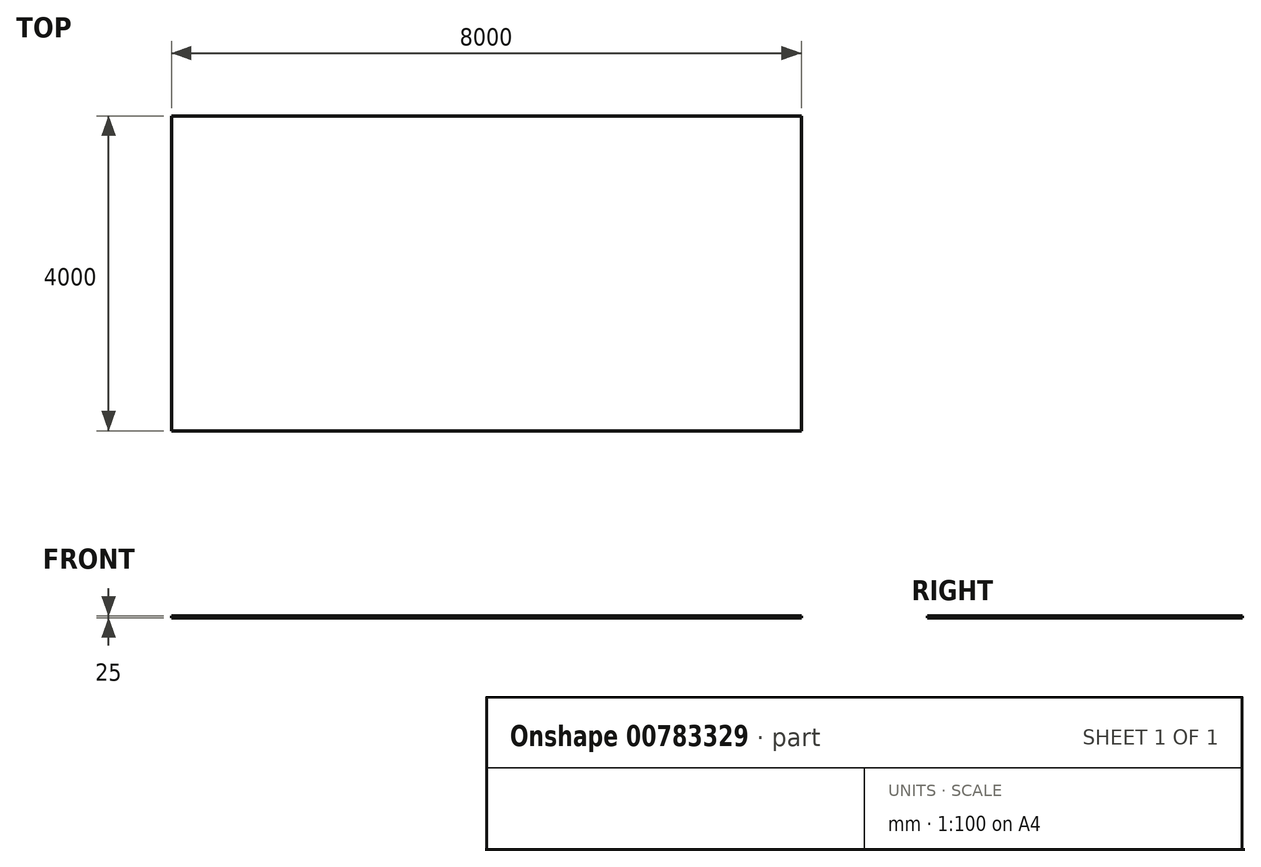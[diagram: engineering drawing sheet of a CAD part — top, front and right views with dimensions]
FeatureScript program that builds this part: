
annotation { "Feature Type Name" : "Feature", "Feature Type Description" : "" }
export const myFeature = defineFeature(function(context is Context, id is Id, definition is map)
    precondition{}
    {
        {
            var Q0;
            Q0=qCreatedBy(makeId("Top.planeOp"),FACE);
            var sketch = newSketch(context, id + "F0", { "sketchPlane" : qUnion([Q0])});
            skLineSegment(sketch, "E0.bottom", {"start": v(0, 0) * mm, "end": v(-8000, 0) * mm});
            skLineSegment(sketch, "E0.top", {"start": v(0, 4000) * mm, "end": v(-8000, 4000) * mm});
            skLineSegment(sketch, "E0.left", {"start": v(0, 0) * mm, "end": v(0, 4000) * mm});
            skLineSegment(sketch, "E0.right", {"start": v(-8000, 0) * mm, "end": v(-8000, 4000) * mm});
            skSolve(sketch);
        }
        {
            var Q0;
            Q0 = qSketchRegion(id + "F0", true);
            extrude(context, id + "F1", {"entities" : qUnion([Q0]), "oppositeDirection" : true, "depth" : 25 * mm, "offsetDistance" : 25 * mm});
        }
    });
